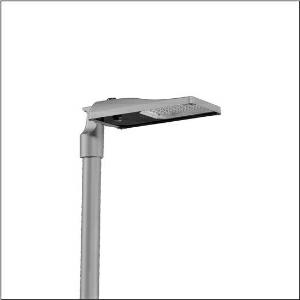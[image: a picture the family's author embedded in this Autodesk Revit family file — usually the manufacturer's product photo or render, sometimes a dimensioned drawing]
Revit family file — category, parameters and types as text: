
# Revit family: streetlight_sl_31_mini___st1_0a_5xh6d31t08ha_30ca
name_source: partatom
category: Lighting Fixtures
units: mm (PartAtom-declared; Revit-internal decimal feet)

## family parameters
Cut with Voids When Loaded = No
Host = Face
Light Source = No
Part Type = Normal
Room Calculation Point = No
Round Connector Dimension = Use Diameter
Shared = No

## types (1)
- --- (1 x LED, 9230 lm, 68.3 W, 3000K)
    Apparent Load = 68 VA
    CIE Flux Codes = 37 72 97 100 100
    Color Rendering = 70
    Color Temperature = 3000K
    Default Elevation = 1800 mm
    Description = Streetlight SL 31 mini D4i, Desk-Remote mast luminaire for post-top, side-entry; light control with lens of PMMA; light distribution: ST1.0a, direct asymmetric distribution, for standard-compliant lighting for roads and squares; LED: luminous flux: 9.230lm, light colour: 730, colour temperature: 3000K; luminous efficacy: 135,1lm/W; control: pre-setting: logarithmic dimming characteristic, flexible luminous flux parameterisation, time-dependent luminous flux control, constant luminous flux control, power reduction, intelligent temperature release in ECG and LED module, overheat protection; luminaire housing, of diecast aluminium, Siteco® metallic grey (DB 702S), corrosivity category C5 high according to DIN EN ISO 12944; cover of toughened safety glass, transparent, opened without tools; mast flange of diecast aluminium, Siteco® metallic grey (DB 702S), spigot size: 76/60mm, mast flange included unmounted; with cable H07RN-F 2x 1.5mm², cable length: 8,5m, connection cable pre-assembled; mains connection: 220..240V, AC, 50/60Hz; power consumption (at start of service life): 68,3W / (at end of service life): 74,5W / (with reduced operation 50%): 29,5W; protection rating (complete): IP66; insulation class (complete): insulation class II (safety insulation); impact resistance: IK09; certification: CE, ENEC, ENEC+, VDE, UKCA, ZD4i; permissible operating ambient temperature for outdoor applications: -40..+50°C; packaging unit: 1 piece

Light Distribution: ST1.0a
    Height = 76 mm
    Lamp = 1 x LED
    Lamp Light Flux = 9230 lm
    Lamp Power = 68.3 W
    Lamp count = 1
    Length = 547 mm
    Luminous efficacy = 135 lm/W
    Manufacturer = Siteco
    ModVariant = No
    Model = 5XH6D31T08HA
    Number of Poles = 1
    OnlyDefault = Yes
    Power Factor = 1
    Product Name = Streetlight SL 31 mini | ST1.0a
    Product group = mast luminaire | pylon top
    ProductGroupID = 6100
    Protection Class = Protection class II
    Protection Degree = IP 66
    RLX_Detail_Level = 1
    RLX_Emergency_Light_Flux = 0 lm
    RLX_Emergency_Type = 0
    RLX_Emergency_Type_DB = No
    RlxData = <blob elided: 24341 chars, md5=e212ef50>
    Socket = socket
    Standby Power = 0 W
    System Light Flux = 9230 lm
    System Power = 68 W
    Type Comments = factory setting: luminous flux: 100 % | dim-lin: 254 | 692 mA
    Type Image = l_1300332.jpg
    URL = http://relux.com
    VarID = @adj_019189
    Voltage = 0 V
    Weight = 0.00 kg
    Width = 265 mm

## geometry (parser evidence)
native form markers: Blend x4, Sweep x9
no freeform markers — native parametric forms only
